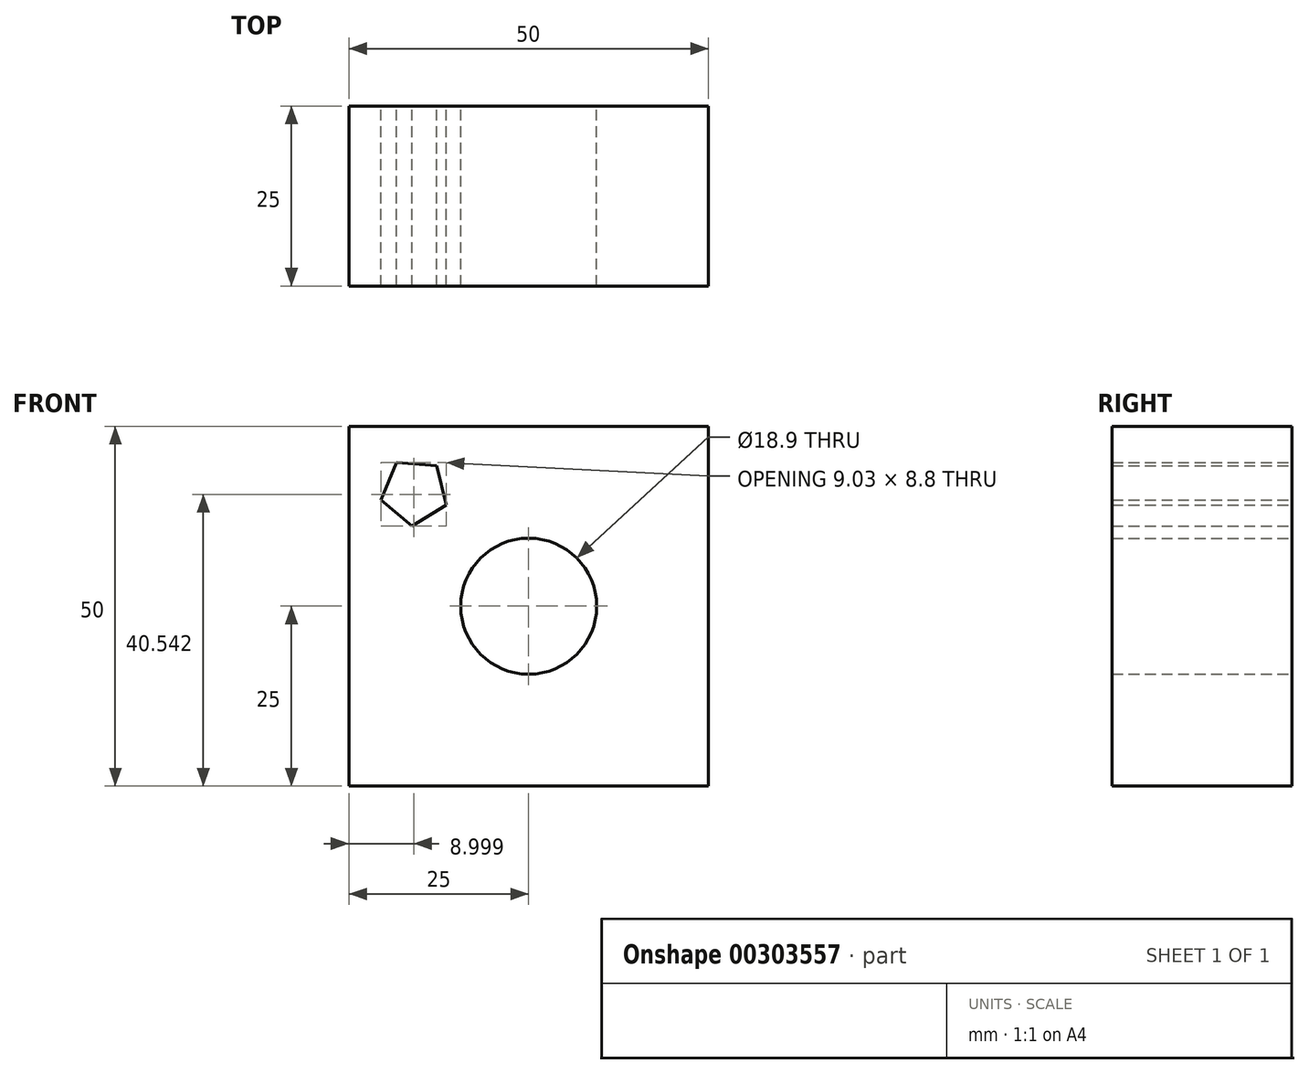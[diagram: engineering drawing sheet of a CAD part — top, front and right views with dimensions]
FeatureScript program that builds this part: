
annotation { "Feature Type Name" : "Feature", "Feature Type Description" : "" }
export const myFeature = defineFeature(function(context is Context, id is Id, definition is map)
    precondition{}
    {
        {
            var Q0;
            Q0=qCreatedBy(makeId("Front.planeOp"),FACE);
            var sketch = newSketch(context, id + "F0", { "sketchPlane" : qUnion([Q0])});
            skLineSegment(sketch, "E0.bottom", {"start": v(0, 0) * mm, "end": v(50, 0) * mm});
            skLineSegment(sketch, "E0.top", {"start": v(0, 50) * mm, "end": v(50, 50) * mm});
            skLineSegment(sketch, "E0.left", {"start": v(0, 0) * mm, "end": v(0, 50) * mm});
            skLineSegment(sketch, "E0.right", {"start": v(50, 0) * mm, "end": v(50, 50) * mm});
            skCircle(sketch, "E1", {"center": v(25, 25) * mm, "radius": 9.45 * mm});
            skPoint(sketch, "E1.centerSnap0", {"position": v(0, 25) * mm});
            skCircle(sketch, "E2.cCircle", {"center": v(9.11, 40.89) * mm, "radius": 3.85 * mm, "construction": true});
            skLineSegment(sketch, "E2.0", {"start": v(12.2, 44.52) * mm, "end": v(13.51, 39.08) * mm});
            skLineSegment(sketch, "E2.1", {"start": v(13.51, 39.08) * mm, "end": v(8.75, 36.14) * mm});
            skLineSegment(sketch, "E2.2", {"start": v(8.75, 36.14) * mm, "end": v(4.48, 39.77) * mm});
            skLineSegment(sketch, "E2.3", {"start": v(4.48, 39.77) * mm, "end": v(6.61, 44.94) * mm});
            skLineSegment(sketch, "E2.4", {"start": v(6.61, 44.94) * mm, "end": v(12.2, 44.52) * mm});
            skPoint(sketch, "E2.0.midPoint", {"position": v(12.85, 41.8) * mm});
            skSolve(sketch);
        }
        {
            var Q0;
            Q0=makeQuery(id+"F0.imprint","IMPRINT",FACE,{"disambiguationData":[TD([[makeQuery(id+"F0.imprint","IMPRINT",EDGE,{"derivedFrom":sQuery(id+"F0.wireOp",EDGE,"E0.bottom")}),1.0]])]});
            extrude(context, id + "F1", {"entities" : qUnion([Q0]), "depth" : 25 * mm});
        }
    });
